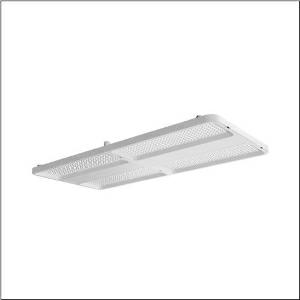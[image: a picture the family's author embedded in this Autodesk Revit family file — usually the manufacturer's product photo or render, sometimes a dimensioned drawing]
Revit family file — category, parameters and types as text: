
# Revit family: highbay_21_maxi_52hn12db4qda
name_source: partatom
category: Lighting Fixtures
units: mm (PartAtom-declared; Revit-internal decimal feet)

## family parameters
Cut with Voids When Loaded = No
Host = Face
Light Source = No
Part Type = Normal
Room Calculation Point = No
Round Connector Dimension = Use Diameter
Shared = No

## types (1)
- --- (1 x LED, 5840 lm, 31.4 W, 4000K)
    Apparent Load = 31 VA
    CIE Flux Codes = 90 98 100 100 100
    Color Rendering = 80
    Color Temperature = 4000K
    Default Elevation = 1800 mm
    Description = high bay luminaire Highbay 21 maxi; direct symmetric wide distribution, light control with lens of PMMA; UGR ≤ 22 (X = 4H | Y = 8H | S = 0.25H | reflection values 70/50/20); luminous flux: 38.000lm; light colour: 840, colour temperature: 4000K, MacAdam ≤ 3 SDCM (initial), colour rendering: CRI > 80; luminous efficacy: 192,2lm/W; rated service life: 75.000h (L80/B50) at AT= ta max; control: DALI 2; housing frame of high-performance plastic PA6, matt traffic white (RAL 9016); cover of PMMA; dimension (LxWxH): 946 x 442 x 72mm; luminaire connection: terminal, 5-pole, max. 2.5mm² (cable entry for one cable, Ø 8.5..16mm); mains connection: 230..240V, AC/DC 0/50..60Hz; connected load: 197,7W; protection rating (complete): IP66; insulation class (complete): insulation class I (protective earthing); protection symbol: D; impact resistance: IK08; halogen-free wiring; for central battery installations according to DIN EN 60598-2-22; LABS conformity tested according to VDMA 24364:2018-05; corresponds to IFS (International Featured Standards) requirements for safety and quality in the food industry; certification: CE, ENEC, VDE, UKCA; permissible operating ambient temperature: -40..+60°C (reducing of maximum allowable ambient temperature of 5°C with ceiling mounting); packaging unit: 1 piece; (delivery without accessories; please order mounting accessories separately)
    Height = 72 mm  [stored 0.23622 ft]
    Lamp = 1 x LED
    Lamp Light Flux = 5840 lm
    Lamp Power = 31.4 W
    Lamp count = 1
    Length = 946 mm
    Luminous efficacy = 186 lm/W
    Manufacturer = Siteco
    ModVariant = No
    Model = 52HN12DB4QDA
    Mounting Place = Ceiling
    Mounting Type = Pendant
    Number of Poles = 1
    OnlyDefault = Yes
    Power Factor = 1
    Product Name = Highbay 21 maxi
    Product group = high bay luminaire
    ProductGroupID = 901
    Protection Class = Protection class I
    Protection Degree = IP 66
    RLX_Detail_Level = 1
    RLX_Emergency_Light_Flux = 0 lm
    RLX_Emergency_Type = 0
    RLX_Emergency_Type_DB = No
    RlxData = <blob elided: 23061 chars, md5=172f9ecd>
    Socket = socket
    Standby Power = 0 W
    System Light Flux = 5840 lm
    System Power = 31 W
    Type Comments = : DC mode (central or group accumulator) initial emergency light level
    Type Image = l_1363244.jpg
    URL = http://relux.com
    VarID = @adj_000561
    Voltage = 0 V
    Weight = 0.00 kg
    Width = 442 mm

note: [stored X ft] marks values corroborated as IEEE doubles in the binary element streams (Revit-internal decimal feet)

## geometry (parser evidence)
native form markers: Blend x4, Sweep x13
no freeform markers — native parametric forms only
